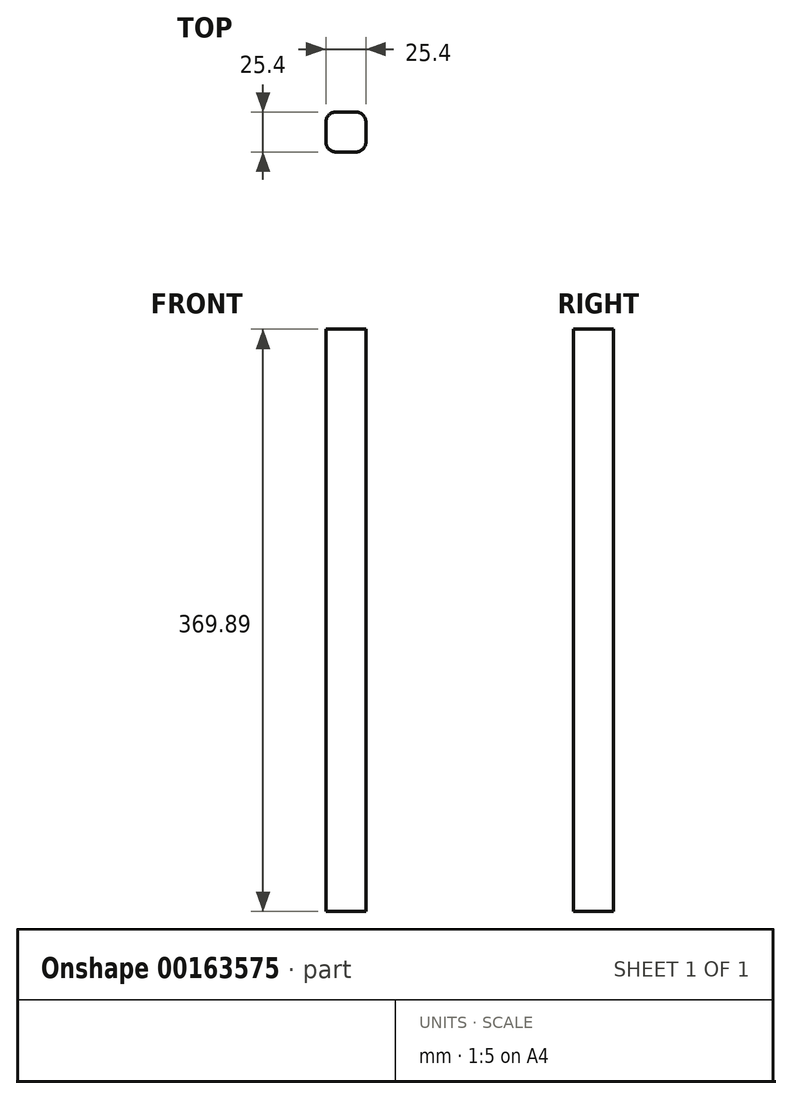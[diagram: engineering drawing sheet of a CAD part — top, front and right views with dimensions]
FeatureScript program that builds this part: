
annotation { "Feature Type Name" : "Feature", "Feature Type Description" : "" }
export const myFeature = defineFeature(function(context is Context, id is Id, definition is map)
    precondition{}
    {
        {
            var Q0;
            Q0=qCreatedBy(makeId("Top.planeOp"),FACE);
            var sketch = newSketch(context, id + "F0", { "sketchPlane" : qUnion([Q0])});
            skLineSegment(sketch, "E0.bottom", {"start": v(6.35, 12.7) * mm, "end": v(-6.35, 12.7) * mm});
            skLineSegment(sketch, "E0.top", {"start": v(6.35, -12.7) * mm, "end": v(-6.35, -12.7) * mm});
            skLineSegment(sketch, "E0.left", {"start": v(12.7, 6.35) * mm, "end": v(12.7, -6.35) * mm});
            skLineSegment(sketch, "E0.right", {"start": v(-12.7, 6.35) * mm, "end": v(-12.7, -6.35) * mm});
            skPoint(sketch, "E0.middle", {"position": v(0, 0) * mm});
            skPoint(sketch, "E1.visualSharp", {"position": v(-12.7, 12.7) * mm});
            skArc(sketch, "E1.filletArc", {"start": v(-6.35, 12.7) * mm, "mid": v(-10.84, 10.84) * mm, "end": v(-12.7, 6.35) * mm});
            skPoint(sketch, "E2.visualSharp", {"position": v(-12.7, -12.7) * mm});
            skArc(sketch, "E2.filletArc", {"start": v(-12.7, -6.35) * mm, "mid": v(-10.84, -10.84) * mm, "end": v(-6.35, -12.7) * mm});
            skPoint(sketch, "E3.visualSharp", {"position": v(12.7, -12.7) * mm});
            skArc(sketch, "E3.filletArc", {"start": v(6.35, -12.7) * mm, "mid": v(10.84, -10.84) * mm, "end": v(12.7, -6.35) * mm});
            skPoint(sketch, "E4.visualSharp", {"position": v(12.7, 12.7) * mm});
            skArc(sketch, "E4.filletArc", {"start": v(12.7, 6.35) * mm, "mid": v(10.84, 10.84) * mm, "end": v(6.35, 12.7) * mm});
            skSolve(sketch);
        }
        {
            var Q0;
            Q0=qSketchRegion(id+"F0",true);
            extrude(context, id + "F1", {"entities" : qUnion([Q0]), "depth" : 369.9 * mm});
        }
    });
